# Revit family: FU_Table_Sandler_Up Table 917-44
name_source: partatom
category: Furniture
units: mm (PartAtom-declared; Revit-internal decimal feet)

## family parameters
Always vertical = Yes
Cut with Voids When Loaded = No
OmniClass Number = 23.40.20.00
OmniClass Title = General Furniture and Specialties
Room Calculation Point = No
Shared = No
Work Plane-Based = No

## types (1)
- Up Table 917.44
    Base = Metal - Chrome - Polished
    Default Elevation = 0 mm  [stored 0 ft]
    Depth = 560 mm  [stored 1.83727 ft]
    Description = Coffee table with frame in black walnut and top in security glass. Base in polished chrome or matt black lacquered finish.
    Frame = Wood - Solid Walnut
    Glass = Glass, Clear Glazing
    Height = 560 mm  [stored 1.83727 ft]
    Manufacturer = Sandler
    Model = Up Table 917.44
    URL = https://www.sandlerseating.com
    Width = 560 mm  [stored 1.83727 ft]

note: [stored X ft] marks values corroborated as IEEE doubles in the binary element streams (Revit-internal decimal feet)

## geometry (parser evidence)
native form markers: Sweep x3
no freeform markers — native parametric forms only
